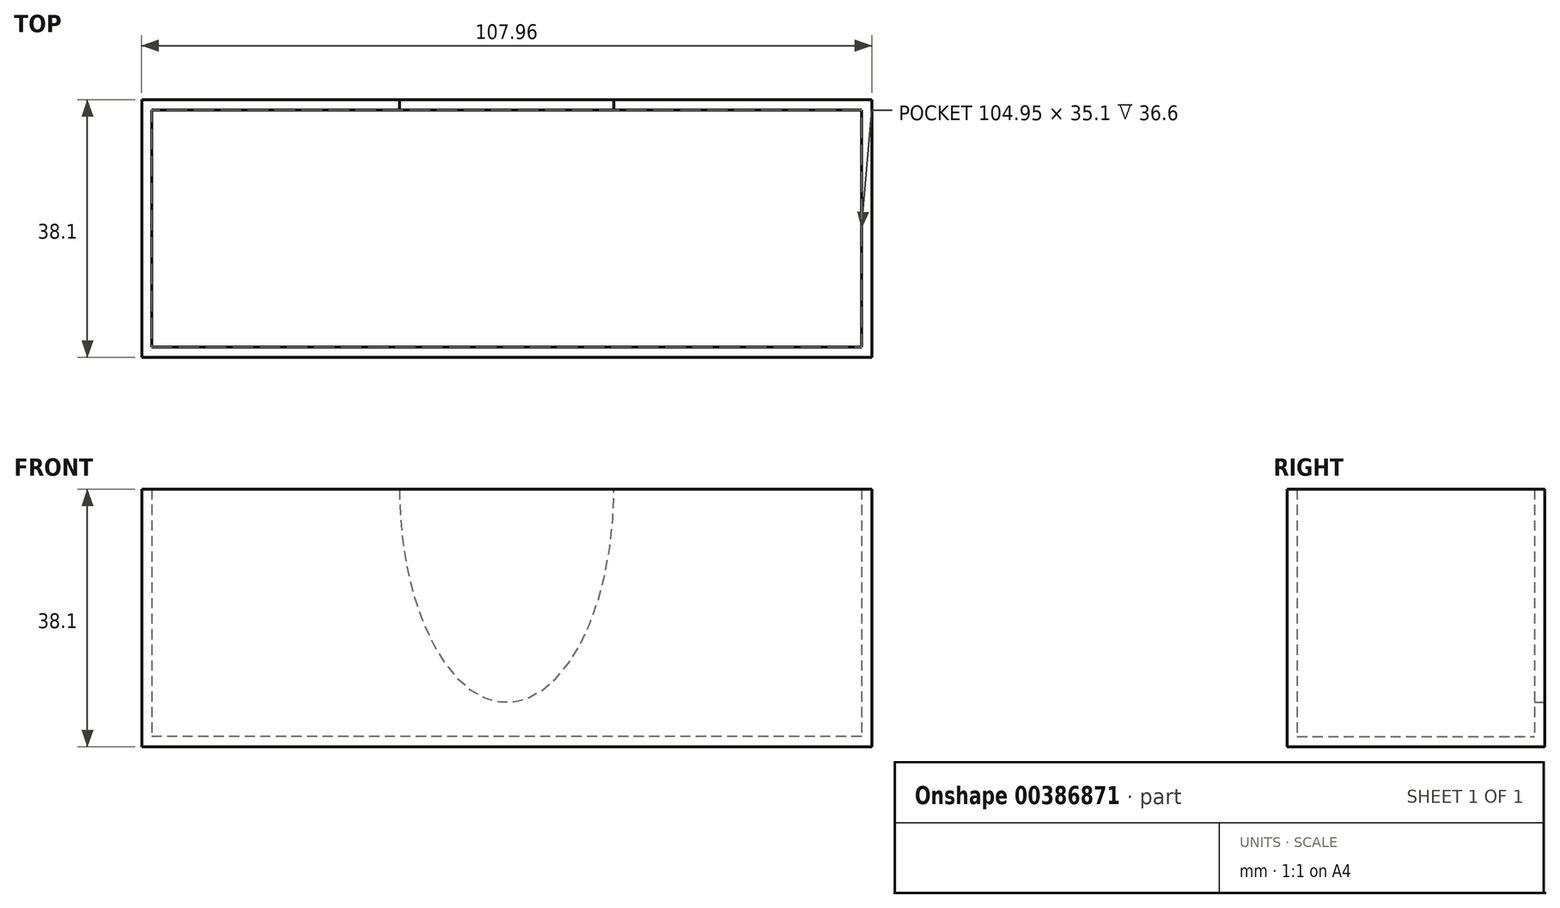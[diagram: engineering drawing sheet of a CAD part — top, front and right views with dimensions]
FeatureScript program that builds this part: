
annotation { "Feature Type Name" : "Feature", "Feature Type Description" : "" }
export const myFeature = defineFeature(function(context is Context, id is Id, definition is map)
    precondition{}
    {
        {
            var Q0;
            Q0=qCreatedBy(makeId("Top.planeOp"),FACE);
            var sketch = newSketch(context, id + "F0", { "sketchPlane" : qUnion([Q0])});
            skLineSegment(sketch, "E0.bottom", {"start": v(53.98, -19.05) * mm, "end": v(-53.98, -19.05) * mm});
            skLineSegment(sketch, "E0.top", {"start": v(53.98, 19.05) * mm, "end": v(-53.98, 19.05) * mm});
            skLineSegment(sketch, "E0.left", {"start": v(53.98, -19.05) * mm, "end": v(53.98, 19.05) * mm});
            skLineSegment(sketch, "E0.right", {"start": v(-53.98, -19.05) * mm, "end": v(-53.98, 19.05) * mm});
            skPoint(sketch, "E0.middle", {"position": v(0, 0) * mm});
            skSolve(sketch);
        }
        {
            var Q0;
            Q0=makeQuery(id+"F0.imprint","IMPRINT",FACE,{"disambiguationData":[TD([[makeQuery(id+"F0.imprint","IMPRINT",EDGE,{"derivedFrom":sQuery(id+"F0.wireOp",EDGE,"E0.bottom")}),-1.0]])]});
            extrude(context, id + "F1", {"entities" : qUnion([Q0]), "depth" : 38.1 * mm, "offsetDistance" : 25.4 * mm});
        }
        {
            var Q0;
            Q0=makeQuery(id+"F1.opExtrude","CAP_FACE",FACE,{"disambiguationData":[OSD([sQuery(id+"F0.wireOp",EDGE,"E0.bottom"),sQuery(id+"F0.wireOp",EDGE,"E0.top"),sQuery(id+"F0.wireOp",EDGE,"E0.left"),sQuery(id+"F0.wireOp",EDGE,"E0.right")])],"isStart":false});
            shell(context, id + "F2", {"entities" : qUnion([Q0]), "thickness" : 1.5 * mm});
        }
        {
            var Q0;
            Q0=qCreatedBy(makeId("Front.planeOp"),FACE);
            var sketch = newSketch(context, id + "F3", { "sketchPlane" : qUnion([Q0])});
            skEllipse(sketch, "E1", {"center": v(0, 38.32) * mm, "majorRadius": 31.75 * mm, "minorRadius": 15.88 * mm, "majorAxis": v(0, -1)});
            skSolve(sketch);
        }
        {
            var Q0;
            Q0 = qSketchRegion(id + "F3", true);
            extrude(context, id + "F4", {"entities" : qUnion([Q0]), "operationType" : NewBodyOperationType.REMOVE, "oppositeDirection" : true, "depth" : 25.4 * mm, "offsetDistance" : 25.4 * mm});
        }
    });
